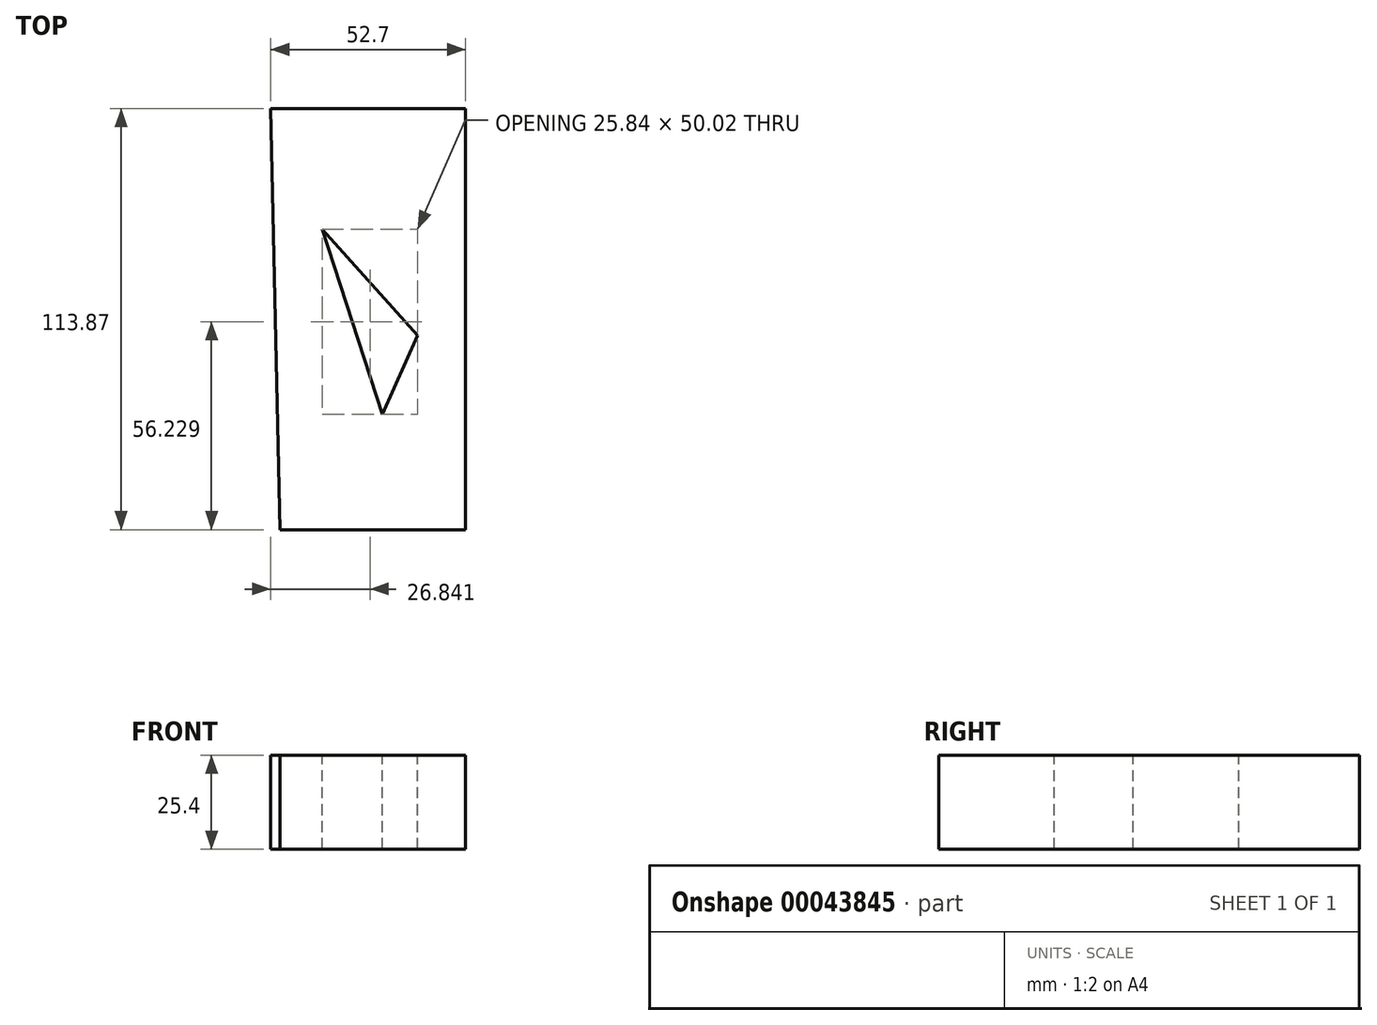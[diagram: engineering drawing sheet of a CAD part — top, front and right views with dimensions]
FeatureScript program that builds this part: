
annotation { "Feature Type Name" : "Feature", "Feature Type Description" : "" }
export const myFeature = defineFeature(function(context is Context, id is Id, definition is map)
    precondition{}
    {
        {
            var Q0;
            Q0=qCreatedBy(makeId("Top.planeOp"),FACE);
            var sketch = newSketch(context, id + "F0", { "sketchPlane" : qUnion([Q0])});
            skLineSegment(sketch, "E0", {"start": v(112.51, 54.94) * mm, "end": v(112.51, -58.93) * mm});
            skLineSegment(sketch, "E1", {"start": v(112.51, -58.93) * mm, "end": v(62.35, -58.93) * mm});
            skLineSegment(sketch, "E2", {"start": v(112.51, 54.94) * mm, "end": v(59.8, 54.94) * mm});
            skLineSegment(sketch, "E3", {"start": v(59.8, 54.94) * mm, "end": v(62.35, -58.93) * mm});
            skSolve(sketch);
        }
        {
            var Q0;
            Q0=makeQuery(id+"F0.imprint","IMPRINT",FACE,{"disambiguationData":[TD([[makeQuery(id+"F0.imprint","IMPRINT",EDGE,{"derivedFrom":sQuery(id+"F0.wireOp",EDGE,"E0")}),-1.0]])]});
            extrude(context, id + "F1", {"entities" : qUnion([Q0]), "depth" : 25.4 * mm});
        }
        {
            var Q0;
            Q0=makeQuery(id+"F1.opExtrude","CAP_FACE",FACE,{"disambiguationData":[OSD([sQuery(id+"F0.wireOp",EDGE,"E0"),sQuery(id+"F0.wireOp",EDGE,"E1"),sQuery(id+"F0.wireOp",EDGE,"E2"),sQuery(id+"F0.wireOp",EDGE,"E3")])],"isStart":false});
            var sketch = newSketch(context, id + "F2", { "sketchPlane" : qUnion([Q0])});
            skLineSegment(sketch, "E4", {"start": v(73.73, 22.3) * mm, "end": v(90.03, -27.7) * mm});
            skLineSegment(sketch, "E5", {"start": v(90.03, -27.7) * mm, "end": v(99.57, -6.36) * mm});
            skLineSegment(sketch, "E6", {"start": v(99.57, -6.36) * mm, "end": v(73.73, 22.3) * mm});
            skLineSegment(sketch, "E7", {"start": v(-34.38, 214.85) * mm, "end": v(-5.98, 214.85) * mm});
            skSolve(sketch);
        }
        {
            var Q0;
            Q0=makeQuery(id+"F2.imprint","IMPRINT",FACE,{"disambiguationData":[TD([[makeQuery(id+"F2.imprint","IMPRINT",EDGE,{"derivedFrom":sQuery(id+"F2.wireOp",EDGE,"E4")}),1.0]])]});
            extrude(context, id + "F3", {"entities" : qUnion([Q0]), "operationType" : NewBodyOperationType.REMOVE, "oppositeDirection" : true, "depth" : 25.4 * mm});
        }
    });
